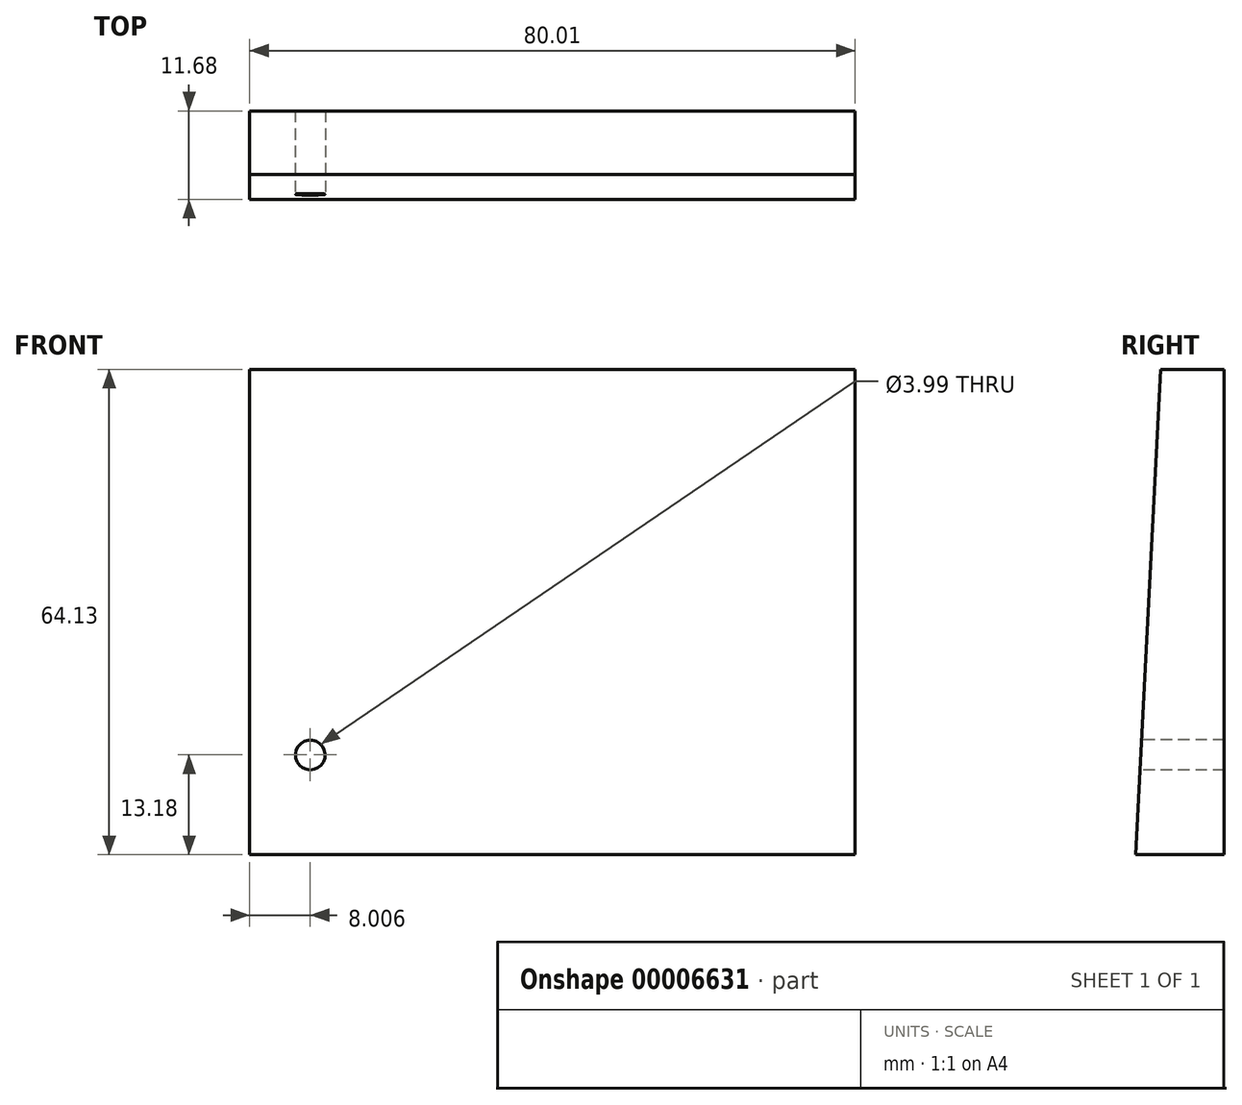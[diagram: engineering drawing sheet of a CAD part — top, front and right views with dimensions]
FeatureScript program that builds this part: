
annotation { "Feature Type Name" : "Feature", "Feature Type Description" : "" }
export const myFeature = defineFeature(function(context is Context, id is Id, definition is map)
    precondition{}
    {
        {
            var Q0;
            Q0=qCreatedBy(makeId("Front.planeOp"),FACE);
            var sketch = newSketch(context, id + "F0", { "sketchPlane" : qUnion([Q0])});
            skCircle(sketch, "E0", {"center": v(0, 0) * mm, "radius": 30 * mm});
            skCircle(sketch, "E1", {"center": v(32, -17.78) * mm, "radius": 2 * mm});
            skCircle(sketch, "E2.0.MirrorC", {"center": v(-32, -17.78) * mm, "radius": 2 * mm});
            skLineSegment(sketch, "E3.bottom", {"start": v(-40, 33.17) * mm, "end": v(40, 33.17) * mm});
            skLineSegment(sketch, "E3.top", {"start": v(-40, -30.96) * mm, "end": v(40, -30.96) * mm});
            skLineSegment(sketch, "E3.left", {"start": v(-40, 33.17) * mm, "end": v(-40, -30.96) * mm});
            skLineSegment(sketch, "E3.right", {"start": v(40, 33.17) * mm, "end": v(40, -30.96) * mm});
            skLineSegment(sketch, "E4", {"start": v(0, 48.55) * mm, "end": v(0, -62.23) * mm, "construction": true});
            skLineSegment(sketch, "E5", {"start": v(-46.63, 30) * mm, "end": v(40.83, 30) * mm, "construction": true});
            skPoint(sketch, "E6", {"position": v(0, 33.17) * mm});
            skSolve(sketch);
        }
        {
            var Q0;
            Q0=makeQuery(id+"F0.imprint","IMPRINT",FACE,{"disambiguationData":[TD([[makeQuery(id+"F0.imprint","IMPRINT",EDGE,{"derivedFrom":sQuery(id+"F0.wireOp",EDGE,"E0")}),1.0]])]});
            extrude(context, id + "F1", {"entities" : qUnion([Q0]), "oppositeDirection" : true, "depth" : 3.8 * mm});
        }
        {
            var Q0;
            Q0=makeQuery(id+"F0.imprint","IMPRINT",FACE,{"disambiguationData":[TD([[makeQuery(id+"F0.imprint","IMPRINT",EDGE,{"derivedFrom":sQuery(id+"F0.wireOp",EDGE,"E2.0.MirrorC")}),-1.0]])]});
            var Q1;
            Q1=makeQuery(id+"F0.imprint","IMPRINT",FACE,{"disambiguationData":[TD([[makeQuery(id+"F0.imprint","IMPRINT",EDGE,{"derivedFrom":sQuery(id+"F0.wireOp",EDGE,"E1")}),1.0]])]});
            var Q2;
            Q2=sQuery(id+"F0.wireOp",EDGE,"E2.0.MirrorC");
            var Q3;
            Q3=sQuery(id+"F0.wireOp",EDGE,"E1");
            extrude(context, id + "F2", {"entities" : qUnion([Q0, Q1]), "operationType" : NewBodyOperationType.ADD, "surfaceEntities" : qUnion([Q2, Q3]), "oppositeDirection" : true, "depth" : 8.9 * mm});
        }
        {
            var Q0;
            Q0=makeQuery(id+"F0.imprint","IMPRINT",FACE,{"disambiguationData":[TD([[makeQuery(id+"F0.imprint","IMPRINT",EDGE,{"derivedFrom":sQuery(id+"F0.wireOp",EDGE,"E0")}),-1.0]])]});
            var Q1;
            Q1=makeQuery(id+"F0.imprint","IMPRINT",FACE,{"disambiguationData":[TD([[makeQuery(id+"F0.imprint","IMPRINT",EDGE,{"derivedFrom":sQuery(id+"F0.wireOp",EDGE,"E0")}),1.0]])]});
            var Q2;
            Q2=makeQuery(id+"F0.imprint","IMPRINT",FACE,{"disambiguationData":[TD([[makeQuery(id+"F0.imprint","IMPRINT",EDGE,{"derivedFrom":sQuery(id+"F0.wireOp",EDGE,"E2.0.MirrorC")}),-1.0]])]});
            var Q3;
            Q3=makeQuery(id+"F0.imprint","IMPRINT",FACE,{"disambiguationData":[TD([[makeQuery(id+"F0.imprint","IMPRINT",EDGE,{"derivedFrom":sQuery(id+"F0.wireOp",EDGE,"E1")}),1.0]])]});
            extrude(context, id + "F3", {"entities" : qUnion([Q0, Q1, Q2, Q3]), "operationType" : NewBodyOperationType.ADD, "depth" : 11.68 * mm});
        }
        {
            var Q0;
            Q0=makeQuery(id+"F3.opExtrude","SWEPT_FACE",FACE,{"disambiguationData":[OSD([sQuery(id+"F0.wireOp",EDGE,"E3.left")])]});
            var sketch = newSketch(context, id + "F4", { "sketchPlane" : qUnion([Q0])});
            skLineSegment(sketch, "E7", {"start": v(8.38, 33.17) * mm, "end": v(11.68, -30.96) * mm});
            skLineSegment(sketch, "E8", {"start": v(11.68, -30.96) * mm, "end": v(0, -30.96) * mm});
            skLineSegment(sketch, "E9", {"start": v(0, -30.96) * mm, "end": v(0, 33.17) * mm});
            skLineSegment(sketch, "E10", {"start": v(0, 33.17) * mm, "end": v(8.38, 33.17) * mm});
            skLineSegment(sketch, "E11", {"start": v(0, 33.17) * mm, "end": v(-12.7, 33.17) * mm});
            skLineSegment(sketch, "E12", {"start": v(-12.7, 33.17) * mm, "end": v(-12.7, -31.24) * mm});
            skLineSegment(sketch, "E13", {"start": v(-12.7, -31.24) * mm, "end": v(0, -30.96) * mm});
            skSolve(sketch);
        }
        {
            var Q0;
            Q0=makeQuery(id+"F4.imprint","IMPRINT",FACE,{"disambiguationData":[TD([[makeQuery(id+"F4.imprint","IMPRINT",EDGE,{"derivedFrom":sQuery(id+"F4.wireOp",EDGE,"E7")}),-1.0]])]});
            var Q1;
            Q1=makeQuery(id+"F4.imprint","IMPRINT",FACE,{"disambiguationData":[TD([[makeQuery(id+"F4.imprint","IMPRINT",EDGE,{"derivedFrom":sQuery(id+"F4.wireOp",EDGE,"E9")}),-1.0]])]});
            extrude(context, id + "F5", {"entities" : qUnion([Q0, Q1]), "operationType" : NewBodyOperationType.INTERSECT, "oppositeDirection" : true, "depth" : 81.28 * mm});
        }
    });
